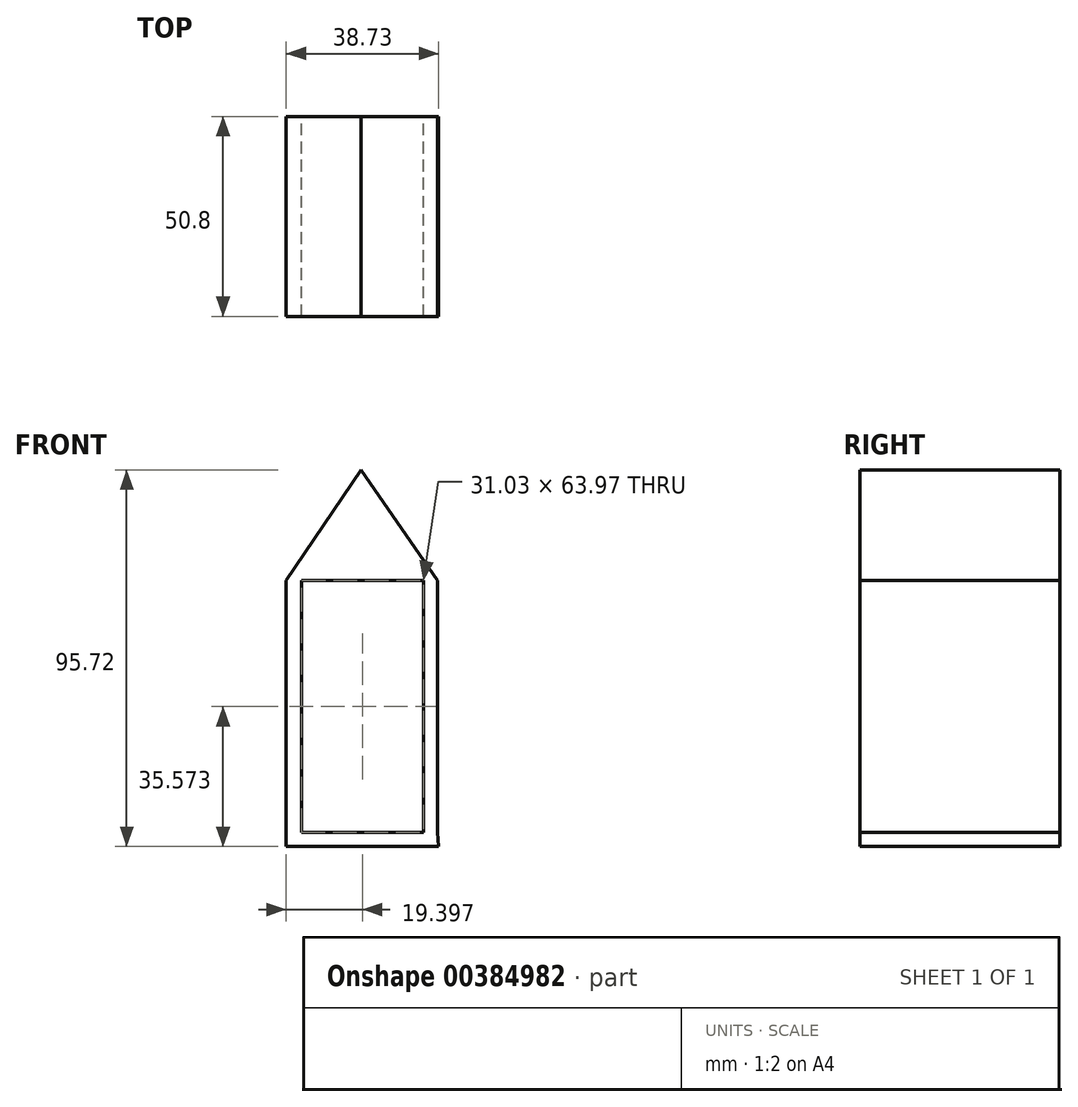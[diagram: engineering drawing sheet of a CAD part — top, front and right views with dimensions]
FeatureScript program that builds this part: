
annotation { "Feature Type Name" : "Feature", "Feature Type Description" : "" }
export const myFeature = defineFeature(function(context is Context, id is Id, definition is map)
    precondition{}
    {
        {
            var Q0;
            Q0=qCreatedBy(makeId("Front.planeOp"),FACE);
            var sketch = newSketch(context, id + "F0", { "sketchPlane" : qUnion([Q0])});
            skLineSegment(sketch, "E0", {"start": v(-16, 22.82) * mm, "end": v(-16, -41.15) * mm});
            skLineSegment(sketch, "E1", {"start": v(-16, -41.15) * mm, "end": v(-12.12, -41.15) * mm});
            skLineSegment(sketch, "E2", {"start": v(-16, 22.82) * mm, "end": v(-12.12, 22.82) * mm});
            skLineSegment(sketch, "E3", {"start": v(-12.12, 22.82) * mm, "end": v(-12.12, -41.15) * mm});
            skLineSegment(sketch, "E4", {"start": v(-12.12, -41.15) * mm, "end": v(18.91, -41.15) * mm});
            skLineSegment(sketch, "E5", {"start": v(18.91, -41.15) * mm, "end": v(18.91, 22.82) * mm});
            skLineSegment(sketch, "E6", {"start": v(18.91, 22.82) * mm, "end": v(-12.12, 22.82) * mm});
            skLineSegment(sketch, "E7", {"start": v(18.91, 22.82) * mm, "end": v(22.42, 22.82) * mm});
            skLineSegment(sketch, "E8", {"start": v(22.42, 22.82) * mm, "end": v(22.42, -41.15) * mm});
            skLineSegment(sketch, "E9", {"start": v(22.42, -41.15) * mm, "end": v(18.91, -41.15) * mm});
            skLineSegment(sketch, "E10", {"start": v(-16, 22.82) * mm, "end": v(3.73, 51.96) * mm});
            skLineSegment(sketch, "E11", {"start": v(2.4, 51.96) * mm, "end": v(22.42, 22.82) * mm});
            skLineSegment(sketch, "E12", {"start": v(-16, -41.15) * mm, "end": v(-16, -41.15) * mm});
            skLineSegment(sketch, "E13", {"start": v(-16, -41.15) * mm, "end": v(22.42, -41.15) * mm});
            skLineSegment(sketch, "E14", {"start": v(-16, -41.15) * mm, "end": v(-16, -44.74) * mm});
            skLineSegment(sketch, "E15", {"start": v(-16, -44.74) * mm, "end": v(22.73, -44.74) * mm});
            skLineSegment(sketch, "E16", {"start": v(22.73, -44.74) * mm, "end": v(22.42, -41.15) * mm});
            skSolve(sketch);
        }
        {
            var Q0;
            Q0 = qSketchRegion(id + "F0", true);
            extrude(context, id + "F1", {"entities" : qUnion([Q0]), "depth" : 50.8 * mm});
        }
    });
